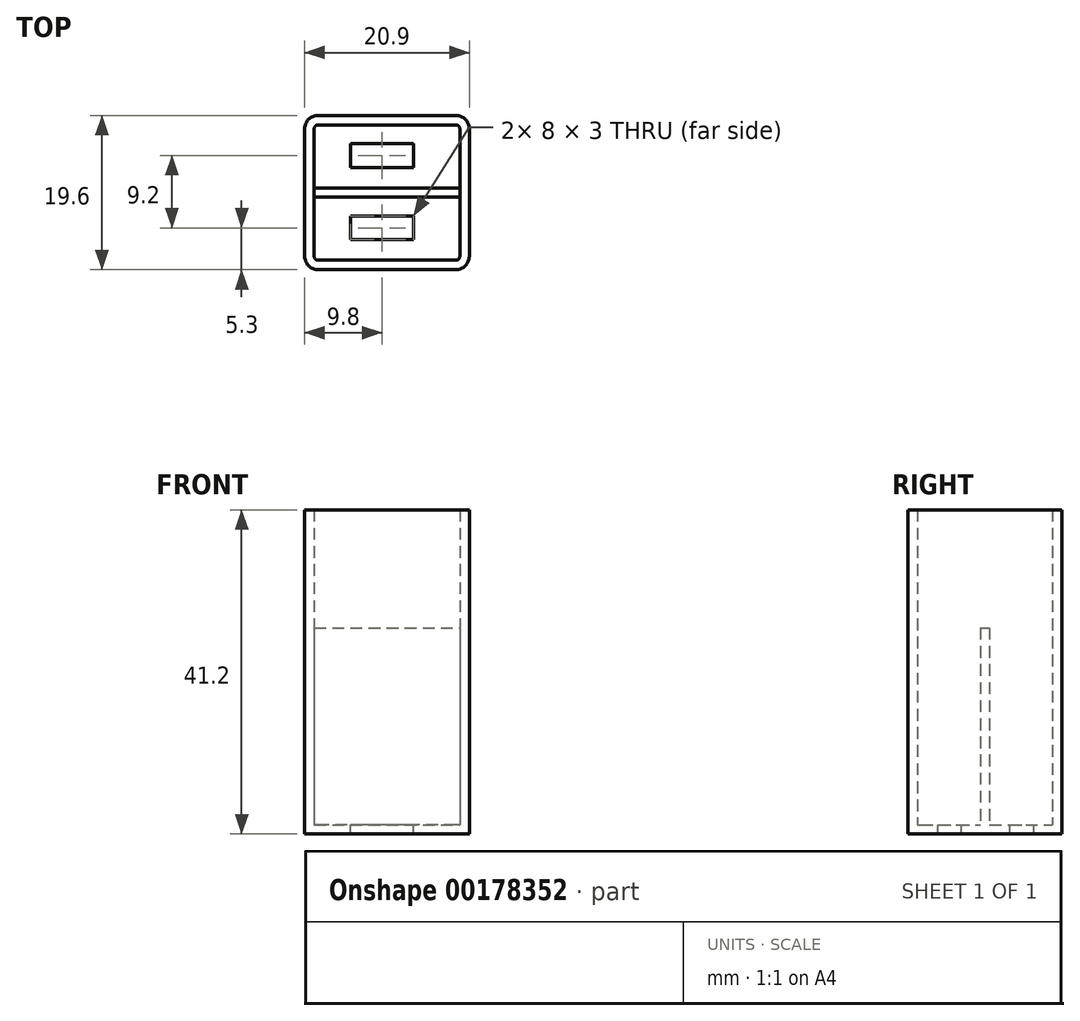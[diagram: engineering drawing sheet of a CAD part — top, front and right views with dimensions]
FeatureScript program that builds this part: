
annotation { "Feature Type Name" : "Feature", "Feature Type Description" : "" }
export const myFeature = defineFeature(function(context is Context, id is Id, definition is map)
    precondition{}
    {
        {
            var Q0;
            Q0=qCreatedBy(makeId("Top.planeOp"),FACE);
            var sketch = newSketch(context, id + "F0", { "sketchPlane" : qUnion([Q0])});
            skLineSegment(sketch, "E0.bottom", {"start": v(8.75, -8.6) * mm, "end": v(-8.75, -8.6) * mm});
            skLineSegment(sketch, "E0.top", {"start": v(8.75, 8.6) * mm, "end": v(-8.75, 8.6) * mm});
            skLineSegment(sketch, "E0.left", {"start": v(9.25, -8.1) * mm, "end": v(9.25, 8.1) * mm});
            skLineSegment(sketch, "E0.right", {"start": v(-9.25, -8.1) * mm, "end": v(-9.25, 8.1) * mm});
            skPoint(sketch, "E0.middle", {"position": v(0, 0) * mm});
            skPoint(sketch, "E1.visualSharp", {"position": v(-9.25, 8.6) * mm});
            skArc(sketch, "E1.filletArc", {"start": v(-8.75, 8.6) * mm, "mid": v(-9.1, 8.45) * mm, "end": v(-9.25, 8.1) * mm});
            skPoint(sketch, "E2.visualSharp", {"position": v(9.25, 8.6) * mm});
            skArc(sketch, "E2.filletArc", {"start": v(9.25, 8.1) * mm, "mid": v(9.1, 8.45) * mm, "end": v(8.75, 8.6) * mm});
            skPoint(sketch, "E3.visualSharp", {"position": v(9.25, -8.6) * mm});
            skArc(sketch, "E3.filletArc", {"start": v(8.75, -8.6) * mm, "mid": v(9.1, -8.45) * mm, "end": v(9.25, -8.1) * mm});
            skPoint(sketch, "E4.visualSharp", {"position": v(-9.25, -8.6) * mm});
            skArc(sketch, "E4.filletArc", {"start": v(-9.25, -8.1) * mm, "mid": v(-9.1, -8.45) * mm, "end": v(-8.75, -8.6) * mm});
            skArc(sketch, "E5.0", {"start": v(10.45, 8.1) * mm, "mid": v(9.95, 9.3) * mm, "end": v(8.75, 9.8) * mm});
            skLineSegment(sketch, "E5.1", {"start": v(10.45, -8.1) * mm, "end": v(10.45, 8.1) * mm});
            skLineSegment(sketch, "E5.2", {"start": v(8.75, 9.8) * mm, "end": v(-8.75, 9.8) * mm});
            skArc(sketch, "E5.3", {"start": v(8.75, -9.8) * mm, "mid": v(9.95, -9.3) * mm, "end": v(10.45, -8.1) * mm});
            skArc(sketch, "E5.4", {"start": v(-8.75, 9.8) * mm, "mid": v(-9.95, 9.3) * mm, "end": v(-10.45, 8.1) * mm});
            skLineSegment(sketch, "E5.5", {"start": v(-10.45, -8.1) * mm, "end": v(-10.45, 8.1) * mm});
            skArc(sketch, "E5.6", {"start": v(-10.45, -8.1) * mm, "mid": v(-9.95, -9.3) * mm, "end": v(-8.75, -9.8) * mm});
            skLineSegment(sketch, "E5.7", {"start": v(8.75, -9.8) * mm, "end": v(-8.75, -9.8) * mm});
            skLineSegment(sketch, "E6", {"start": v(-9.25, 0.6) * mm, "end": v(9.25, 0.6) * mm});
            skLineSegment(sketch, "E7", {"start": v(-9.25, -0.6) * mm, "end": v(9.25, -0.6) * mm});
            skLineSegment(sketch, "E8.bottom", {"start": v(3.35, 3.2) * mm, "end": v(-4.65, 3.2) * mm});
            skLineSegment(sketch, "E8.top", {"start": v(3.35, 6.2) * mm, "end": v(-4.65, 6.2) * mm});
            skLineSegment(sketch, "E8.left", {"start": v(3.35, 3.2) * mm, "end": v(3.35, 6.2) * mm});
            skLineSegment(sketch, "E8.right", {"start": v(-4.65, 3.2) * mm, "end": v(-4.65, 6.2) * mm});
            skPoint(sketch, "E8.middle", {"position": v(-0.65, 4.7) * mm});
            skLineSegment(sketch, "E9.1.0.0", {"start": v(-4.65, -6) * mm, "end": v(-4.65, -3) * mm});
            skLineSegment(sketch, "E9.1.0.1", {"start": v(3.35, -3) * mm, "end": v(-4.65, -3) * mm});
            skLineSegment(sketch, "E9.1.0.2", {"start": v(3.35, -6) * mm, "end": v(-4.65, -6) * mm});
            skLineSegment(sketch, "E9.1.0.3", {"start": v(3.35, -6) * mm, "end": v(3.35, -3) * mm});
            skLineSegment(sketch, "E9.direction1", {"start": v(-4.65, 3.2) * mm, "end": v(-4.65, -6) * mm, "construction": true});
            skSolve(sketch);
        }
        {
            var Q0;
            Q0=makeQuery(id+"F0.imprint","IMPRINT",FACE,{"disambiguationData":[TD([[makeQuery(id+"F0.imprint","IMPRINT",EDGE,{"derivedFrom":sQuery(id+"F0.wireOp",EDGE,"E0.bottom")}),1.0]])]});
            extrude(context, id + "F1", {"entities" : qUnion([Q0]), "depth" : 40 * mm, "hasSecondDirection" : true, "secondDirectionOppositeDirection" : true, "secondDirectionDepth" : 1.2 * mm});
        }
        {
            var Q0;
            Q0=makeQuery(id+"F0.imprint","IMPRINT",FACE,{"disambiguationData":[TD([[makeQuery(id+"F0.imprint","IMPRINT",EDGE,{"derivedFrom":sQuery(id+"F0.wireOp",EDGE,"E0.top")}),1.0]])]});
            var Q1;
            {var subQ0=sQuery(id+"F0.wireOp",EDGE,"E6");Q1=makeQuery(id+"F0.imprint","IMPRINT",FACE,{"disambiguationData":[TD([[makeQuery(id+"F0.imprint","IMPRINT",EDGE,{"derivedFrom":subQ0}),-1.0]])]});}
            var Q2;
            Q2=makeQuery(id+"F0.imprint","IMPRINT",FACE,{"disambiguationData":[TD([[makeQuery(id+"F0.imprint","IMPRINT",EDGE,{"derivedFrom":sQuery(id+"F0.wireOp",EDGE,"E0.bottom")}),-1.0]])]});
            extrude(context, id + "F2", {"entities" : qUnion([Q0, Q1, Q2]), "operationType" : NewBodyOperationType.ADD, "oppositeDirection" : true, "depth" : 1.2 * mm});
        }
        {
            var Q0;
            {var subQ0=sQuery(id+"F0.wireOp",EDGE,"E6");Q0=makeQuery(id+"F0.imprint","IMPRINT",FACE,{"disambiguationData":[TD([[makeQuery(id+"F0.imprint","IMPRINT",EDGE,{"derivedFrom":subQ0}),-1.0]])]});}
            extrude(context, id + "F3", {"entities" : qUnion([Q0]), "operationType" : NewBodyOperationType.ADD, "depth" : 25 * mm});
        }
    });
